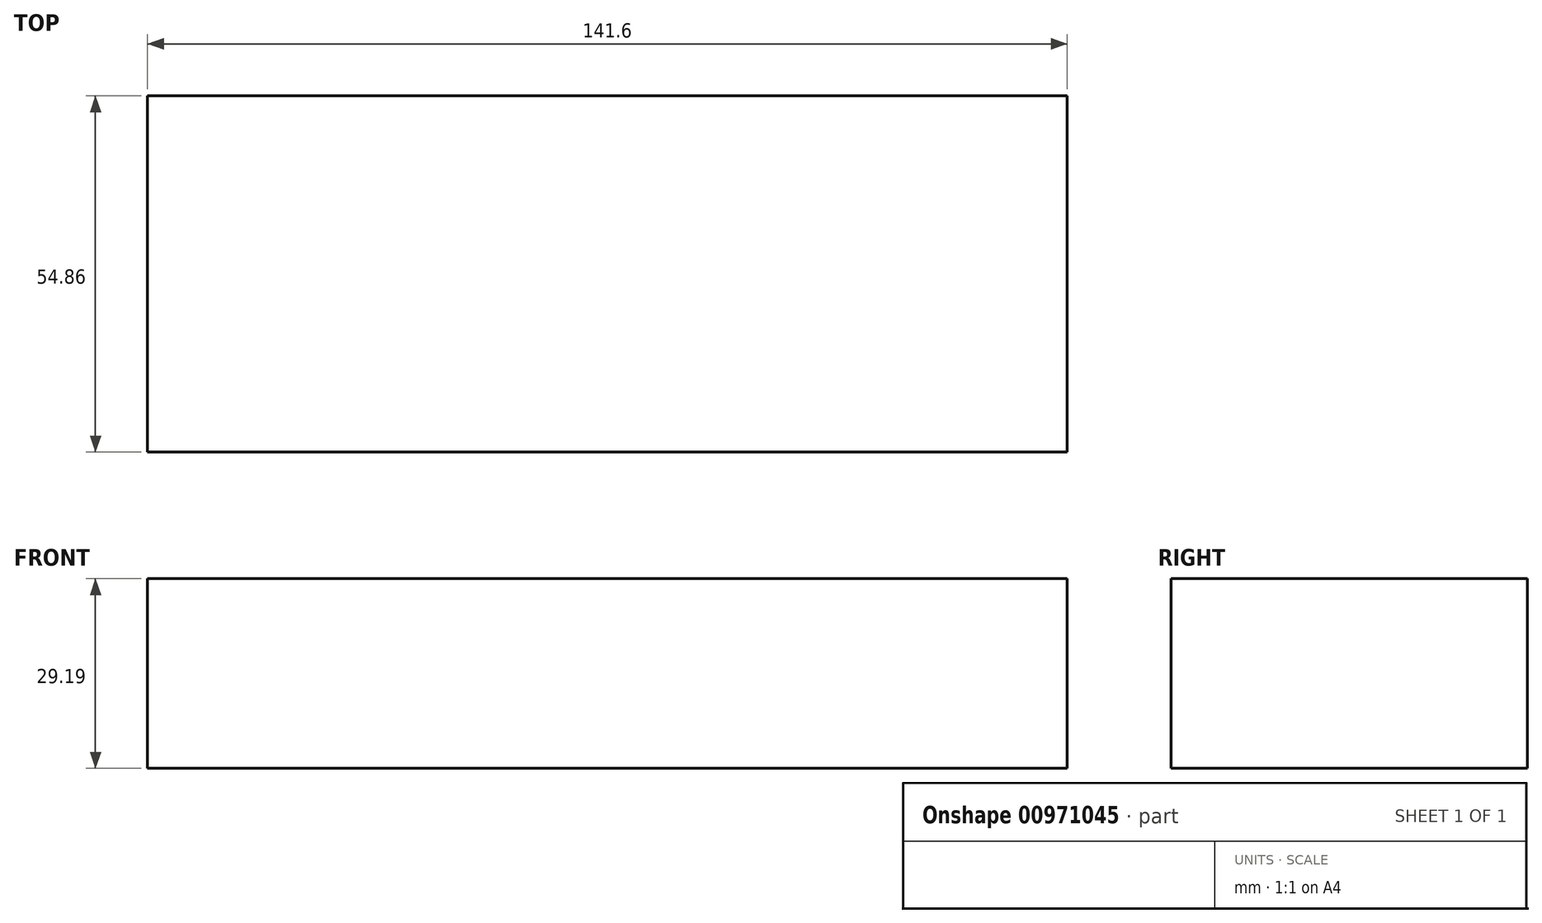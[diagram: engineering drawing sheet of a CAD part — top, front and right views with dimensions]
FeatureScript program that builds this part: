
annotation { "Feature Type Name" : "Feature", "Feature Type Description" : "" }
export const myFeature = defineFeature(function(context is Context, id is Id, definition is map)
    precondition{}
    {
        {
            var Q0;
            Q0=qCreatedBy(makeId("Front.planeOp"),FACE);
            var sketch = newSketch(context, id + "F0", { "sketchPlane" : qUnion([Q0])});
            skLineSegment(sketch, "E0.bottom", {"start": v(-13.75, -4.07) * mm, "end": v(127.85, -4.07) * mm});
            skLineSegment(sketch, "E0.top", {"start": v(-13.75, 25.12) * mm, "end": v(127.85, 25.12) * mm});
            skLineSegment(sketch, "E0.left", {"start": v(-13.75, -4.07) * mm, "end": v(-13.75, 25.12) * mm});
            skLineSegment(sketch, "E0.right", {"start": v(127.85, -4.07) * mm, "end": v(127.85, 25.12) * mm});
            skSolve(sketch);
        }
        {
            var Q0;
            Q0=makeQuery(id+"F0.imprint","IMPRINT",FACE,{"disambiguationData":[TD([[makeQuery(id+"F0.imprint","IMPRINT",EDGE,{"derivedFrom":sQuery(id+"F0.wireOp",EDGE,"E0.bottom")}),1.0]])]});
            extrude(context, id + "F1", {"entities" : qUnion([Q0]), "depth" : 54.86 * mm, "offsetDistance" : 25.4 * mm});
        }
    });
